# Revit family: ALBA_R200ExHGxxSF
name_source: partatom
category: Leuchten
units: mm (PartAtom-declared; Revit-internal decimal feet)

## family parameters
Basisbauteil = Fläche
Beim Laden mit Abzugskörper schneiden = Nein
Bemaßung runder Anschluss = Durchmesser verwenden
Gemeinsam genutzt = Nein
Lichtquelle = Ja
OmniClass-Nummer = 23.80.70.11
OmniClass-Titel = Luminaries for Internal Lighting
Raumberechnungspunkt = Nein
Teiletyp = Normal

## types (16) — shared parameters
Baugruppenkennzeichen = D5020200
Datei für fotometrisches Netz = Master_ALBA_R200E_HG_Diffusor.IES
Emissionsform beim Rendern sichtbar = Nein
Farbfilter = 16777215
Farbtemperaturverschiebung bei Dämpfen der Lampe = <Keine Auswahl>
Hersteller = RIDI Leuchten GmbH
Lampe = LED
Neigungswinkel = 90.00°
URL = www.ridi.de
Von Kreisdurchmesser aussenden = 182 mm  [stored 0.597113 ft]
brand = RIDI
conformity mark = CE
electrical safety class = 2
height = 101 mm  [stored 0.331365 ft]
ingress protection (IP) code = IP20
length = 208 mm
nominal frequency = 50-60Hz
nominal voltage = 230
voltage type (AC, DC, UC) = AC
weight = 0.81 kg
width = 208 mm
zero-valued in all types: Vorgabe-Ansicht

## per-type parameters (varying)
| type | Modell | Scheinlast | rated input power |
| ALBA R200E NDHG830SF0250OS | 0322145 | 17 VA | 17 |
| ALBA R200E NDHG830SF0350OS | 0322157 | 26 VA | 26 |
| ALBA R200E NDHG840SF0250OS | 0322146 | 17 VA | 17 |
| ALBA R200E NDHG840SF0350OS | 0322158 | 26 VA | 26 |
| ALBA R200E NDHG930SF0200OS | 0322386 | 17 VA | 17 |
| ALBA R200E NDHG940SF0225OS | 0322387 | 17 VA | 17 |
| ALBA R200E NDHG930SF0300OS | 0322422 | 26 VA | 26 |
| ALBA R200E NDHG940SF0300OS | 0322423 | 26 VA | 26 |
| ALBA R200E DAHG830SF0250OS | 0332145 | 17 VA | 17 |
| ALBA R200E DAHG840SF0250OS | 0332146 | 17 VA | 17 |
| ALBA R200E DAHG830SF0350OS | 0332157 | 26 VA | 26 |
| ALBA R200E DAHG840SF0350OS | 0332158 | 26 VA | 26 |
| ALBA R200E DAHG930SF0200OS | 0332386 | 17 VA | 17 |
| ALBA R200E DAHG940SF0225OS | 0332387 | 17 VA | 17 |
| ALBA R200E DAHG930SF0300OS | 0332422 | 26 VA | 26 |
| ALBA R200E DAHG940SF0300OS | 0332423 | 26 VA | 26 |

note: column(s) folded — value = type name in every type: product name

note: [stored X ft] marks values corroborated as IEEE doubles in the binary element streams (Revit-internal decimal feet)
